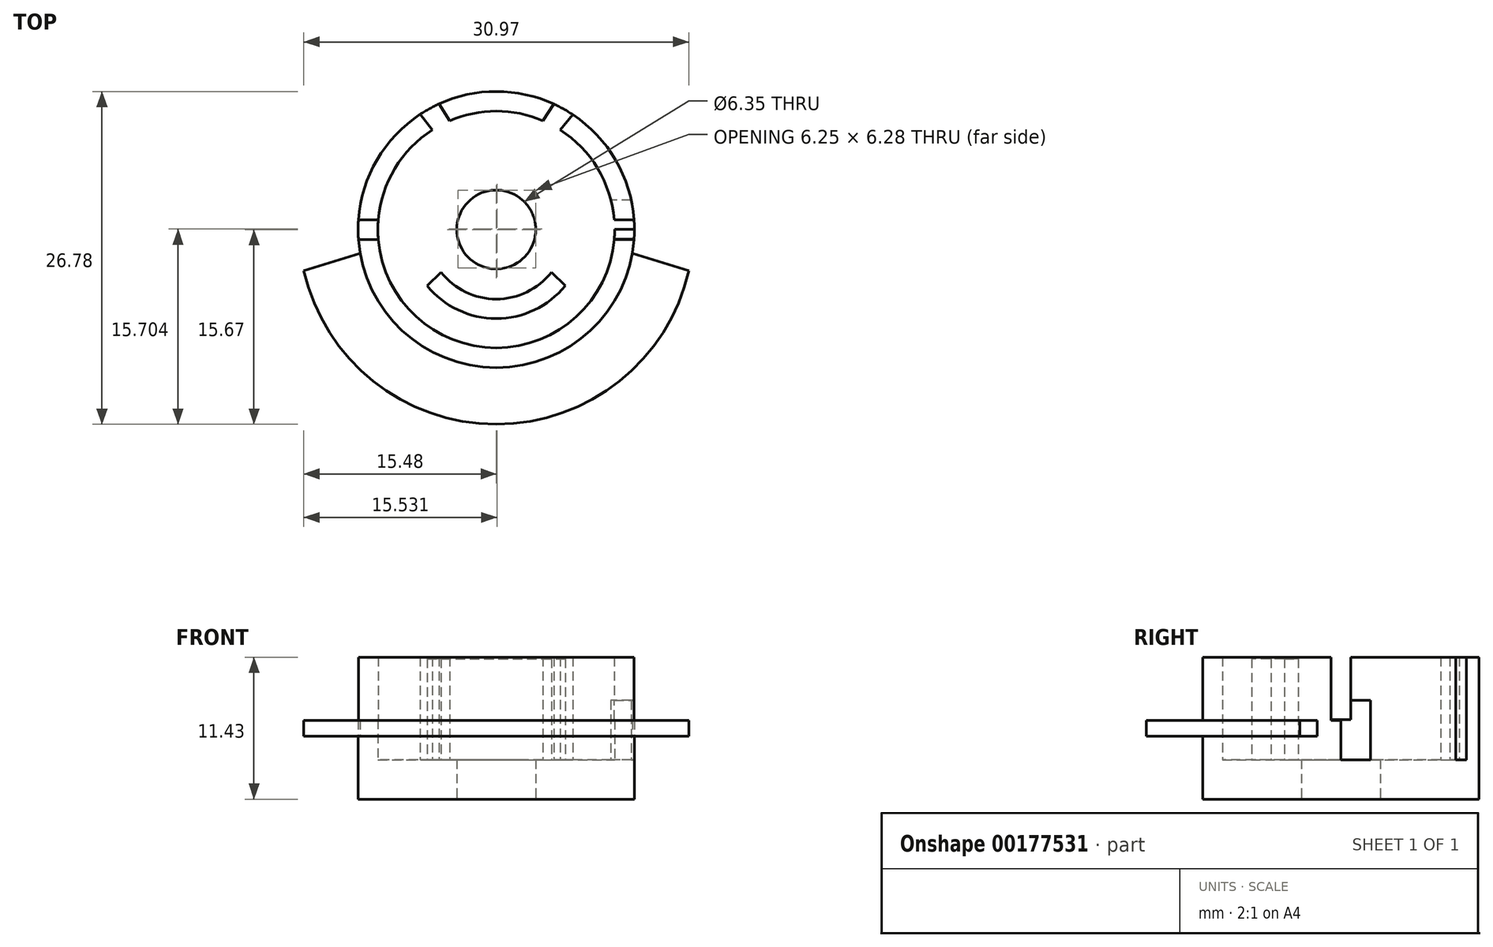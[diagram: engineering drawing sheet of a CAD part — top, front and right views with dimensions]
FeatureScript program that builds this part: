
annotation { "Feature Type Name" : "Feature", "Feature Type Description" : "" }
export const myFeature = defineFeature(function(context is Context, id is Id, definition is map)
    precondition{}
    {
        {
            var Q0;
            Q0=qCreatedBy(makeId("Top.planeOp"),FACE);
            var sketch = newSketch(context, id + "F0", { "sketchPlane" : qUnion([Q0])});
            skCircle(sketch, "E0", {"center": v(0, 0) * mm, "radius": 11.11 * mm});
            skSolve(sketch);
        }
        {
            var Q0;
            Q0=qSketchRegion(id+"F0",true);
            extrude(context, id + "F1", {"entities" : qUnion([Q0]), "depth" : 3.17 * mm});
        }
        {
            var Q0;
            Q0=qCreatedBy(makeId("Top.planeOp"),FACE);
            var sketch = newSketch(context, id + "F2", { "sketchPlane" : qUnion([Q0])});
            skCircle(sketch, "E1", {"center": v(0, 0) * mm, "radius": 3.17 * mm});
            skSolve(sketch);
        }
        {
            var Q0;
            Q0=qSketchRegion(id+"F2",true);
            extrude(context, id + "F3", {"entities" : qUnion([Q0]), "operationType" : NewBodyOperationType.REMOVE, "depth" : 71.12 * mm});
        }
        {
            var Q0;
            Q0=qCreatedBy(makeId("Top.planeOp"),FACE);
            cPlane(context, id + "F4", {"entities" : qUnion([Q0]), "cplaneType" : CPlaneType.OFFSET, "offset" : 3.17 * mm, "width" : 152.4 * mm, "height" : 152.4 * mm});
        }
        {
            var Q0;
            Q0=qCreatedBy(id+"F4.planeOp",FACE);
            var sketch = newSketch(context, id + "F5", { "sketchPlane" : qUnion([Q0])});
            skCircle(sketch, "E2", {"center": v(0, 0) * mm, "radius": 11.11 * mm});
            skSolve(sketch);
        }
        {
            var Q0;
            Q0=qSketchRegion(id+"F5",true);
            extrude(context, id + "F6", {"entities" : qUnion([Q0]), "operationType" : NewBodyOperationType.ADD, "depth" : 8.25 * mm});
        }
        {
            var Q0;
            Q0=qCreatedBy(id+"F4.planeOp",FACE);
            var sketch = newSketch(context, id + "F7", { "sketchPlane" : qUnion([Q0])});
            skCircle(sketch, "E3", {"center": v(0, 0) * mm, "radius": 9.53 * mm});
            skSolve(sketch);
        }
        {
            var Q0;
            Q0=qSketchRegion(id+"F7",true);
            extrude(context, id + "F8", {"entities" : qUnion([Q0]), "operationType" : NewBodyOperationType.REMOVE, "depth" : 25.4 * mm});
        }
        {
            var Q0;
            Q0=qCreatedBy(id+"F4.planeOp",FACE);
            cPlane(context, id + "F9", {"entities" : qUnion([Q0]), "cplaneType" : CPlaneType.OFFSET, "offset" : 3.17 * mm, "width" : 152.4 * mm, "height" : 152.4 * mm});
        }
        {
            var Q0;
            Q0=qCreatedBy(makeId("Right.planeOp"),FACE);
            var sketch = newSketch(context, id + "F10", { "sketchPlane" : qUnion([Q0])});
            skLineSegment(sketch, "E4", {"start": v(0, 6.4) * mm, "end": v(-0.8, 6.4) * mm});
            skLineSegment(sketch, "E5", {"start": v(0, 6.4) * mm, "end": v(0.8, 6.4) * mm});
            skLineSegment(sketch, "E6", {"start": v(-0.8, 6.4) * mm, "end": v(-0.8, 14.02) * mm});
            skLineSegment(sketch, "E7", {"start": v(0.8, 6.4) * mm, "end": v(0.8, 14.02) * mm});
            skLineSegment(sketch, "E8", {"start": v(0.8, 14.02) * mm, "end": v(-0.8, 14.02) * mm});
            skSolve(sketch);
        }
        {
            var Q0;
            Q0=qSketchRegion(id+"F10",true);
            extrude(context, id + "F11", {"entities" : qUnion([Q0]), "operationType" : NewBodyOperationType.REMOVE, "oppositeDirection" : true, "depth" : 25.4 * mm, "hasSecondDirection" : true, "secondDirectionOppositeDirection" : false, "secondDirectionDepth" : 25.4 * mm});
        }
        {
            var Q0;
            Q0=qCreatedBy(makeId("Right.planeOp"),FACE);
            var sketch = newSketch(context, id + "F12", { "sketchPlane" : qUnion([Q0])});
            skLineSegment(sketch, "E9", {"start": v(-0.79, 7.95) * mm, "end": v(0.8, 7.95) * mm});
            skLineSegment(sketch, "E10", {"start": v(-0.79, 6.35) * mm, "end": v(-0.79, 7.95) * mm});
            skLineSegment(sketch, "E11", {"start": v(-0.79, 6.35) * mm, "end": v(0, 6.35) * mm});
            skPoint(sketch, "E12.start.orphan", {"position": v(0.8, 7.95) * mm});
            skPoint(sketch, "E13.endSnap0", {"position": v(0.8, 4.53) * mm});
            skPoint(sketch, "E14.orphan", {"position": v(0.8, 2.72) * mm});
            skPoint(sketch, "E15.orphan", {"position": v(2.38, 7.95) * mm});
            skLineSegment(sketch, "E16", {"start": v(0, 6.35) * mm, "end": v(0, 4.77) * mm});
            skPoint(sketch, "E17.start.orphan", {"position": v(0.8, 6.35) * mm});
            skPoint(sketch, "E18.start.orphan", {"position": v(0.8, 4.78) * mm});
            skLineSegment(sketch, "E19", {"start": v(0.8, 7.95) * mm, "end": v(2.38, 7.95) * mm});
            skLineSegment(sketch, "E20", {"start": v(2.38, 4.77) * mm, "end": v(2.38, 7.95) * mm});
            skLineSegment(sketch, "E21", {"start": v(0, 4.77) * mm, "end": v(0, 3.17) * mm});
            skLineSegment(sketch, "E22", {"start": v(2.38, 4.77) * mm, "end": v(2.38, 3.17) * mm});
            skLineSegment(sketch, "E23", {"start": v(2.38, 3.17) * mm, "end": v(0, 3.17) * mm});
            skSolve(sketch);
        }
        {
            var Q0;
            Q0=qSketchRegion(id+"F12",true);
            extrude(context, id + "F13", {"entities" : qUnion([Q0]), "operationType" : NewBodyOperationType.REMOVE, "depth" : 25.4 * mm});
        }
        {
            var Q0;
            Q0=qCreatedBy(id+"F9.planeOp",FACE);
            var sketch = newSketch(context, id + "F14", { "sketchPlane" : qUnion([Q0])});
            skLineSegment(sketch, "E24", {"start": v(0, 0) * mm, "end": v(0, 11.18) * mm, "construction": true});
            skLineSegment(sketch, "E25", {"start": v(0, 11.18) * mm, "end": v(0, 8) * mm, "construction": true});
            skLineSegment(sketch, "E26", {"start": v(0, 8) * mm, "end": v(-5.06, 8) * mm, "construction": true});
            skLineSegment(sketch, "E27", {"start": v(0, 8) * mm, "end": v(4.84, 8) * mm, "construction": true});
            skLineSegment(sketch, "E28", {"start": v(5.11, 8) * mm, "end": v(6.3, 9.4) * mm});
            skLineSegment(sketch, "E29", {"start": v(5.11, 8) * mm, "end": v(3.72, 8.74) * mm});
            skLineSegment(sketch, "E30", {"start": v(3.72, 8.74) * mm, "end": v(4.7, 10.2) * mm});
            skLineSegment(sketch, "E31", {"start": v(4.7, 10.2) * mm, "end": v(6.3, 9.4) * mm});
            skLineSegment(sketch, "E32", {"start": v(-5.13, 8) * mm, "end": v(-6.22, 9.4) * mm});
            skLineSegment(sketch, "E33", {"start": v(-5.13, 8) * mm, "end": v(-3.73, 8.73) * mm});
            skLineSegment(sketch, "E34", {"start": v(-3.73, 8.73) * mm, "end": v(-4.7, 10.25) * mm});
            skLineSegment(sketch, "E35", {"start": v(-4.7, 10.25) * mm, "end": v(-6.22, 9.4) * mm});
            skSolve(sketch);
        }
        {
            var Q0;
            Q0=qSketchRegion(id+"F14",true);
            extrude(context, id + "F15", {"entities" : qUnion([Q0]), "operationType" : NewBodyOperationType.REMOVE, "depth" : 25.4 * mm, "hasSecondDirection" : true, "secondDirectionOppositeDirection" : true, "secondDirectionDepth" : 3.17 * mm});
        }
        {
            var Q0;
            Q0=qCreatedBy(id+"F4.planeOp",FACE);
            var sketch = newSketch(context, id + "F16", { "sketchPlane" : qUnion([Q0])});
            skLineSegment(sketch, "E36", {"start": v(0, -7.18) * mm, "end": v(0, -7.17) * mm, "construction": true});
            skPoint(sketch, "E37.second.point", {"position": v(0, 15.02) * mm});
            skPoint(sketch, "E37.third.point", {"position": v(-11.08, 5.03) * mm});
            skArc(sketch, "E38", {"start": v(-5.55, -4.53) * mm, "mid": v(0, -7.17) * mm, "end": v(5.55, -4.53) * mm});
            skArc(sketch, "E39", {"start": v(-4.43, -3.44) * mm, "mid": v(0, -5.6) * mm, "end": v(4.43, -3.44) * mm});
            skLineSegment(sketch, "E40", {"start": v(5.55, -4.53) * mm, "end": v(4.43, -3.44) * mm});
            skLineSegment(sketch, "E41", {"start": v(-4.43, -3.44) * mm, "end": v(-5.55, -4.53) * mm});
            skLineSegment(sketch, "E42.trimOffspring", {"start": v(0, -5.6) * mm, "end": v(0, -5.6) * mm, "construction": true});
            skSolve(sketch);
        }
        {
            var Q0;
            Q0=qSketchRegion(id+"F16",true);
            extrude(context, id + "F17", {"entities" : qUnion([Q0]), "operationType" : NewBodyOperationType.ADD, "depth" : 8.13 * mm});
        }
        {
            var Q0;
            Q0=qCreatedBy(makeId("Top.planeOp"),FACE);
            cPlane(context, id + "F18", {"entities" : qUnion([Q0]), "cplaneType" : CPlaneType.OFFSET, "offset" : 6.35 * mm, "width" : 152.4 * mm, "height" : 152.4 * mm});
        }
        {
            var Q0;
            Q0=qCreatedBy(id+"F18.planeOp",FACE);
            var sketch = newSketch(context, id + "F19", { "sketchPlane" : qUnion([Q0])});
            skLineSegment(sketch, "E43", {"start": v(10.94, -1.92) * mm, "end": v(15.5, -3.32) * mm});
            skLineSegment(sketch, "E44", {"start": v(-10.93, -1.92) * mm, "end": v(-15.48, -3.32) * mm});
            skArc(sketch, "E45", {"start": v(-15.48, -3.32) * mm, "mid": v(0, -15.67) * mm, "end": v(15.5, -3.32) * mm});
            skArc(sketch, "E46", {"start": v(-10.93, -1.92) * mm, "mid": v(0, -10.31) * mm, "end": v(10.94, -1.92) * mm});
            skSolve(sketch);
        }
        {
            var Q0;
            Q0=qSketchRegion(id+"F19",true);
            extrude(context, id + "F20", {"entities" : qUnion([Q0]), "operationType" : NewBodyOperationType.ADD, "oppositeDirection" : true, "depth" : 1.27 * mm});
        }
    });
